# Revit family: 4068363 Lighting Fixture_Sylvania_Glace Square_Surface Mounted
name_source: partatom
category: Lighting Fixtures
revit_build: Autodesk Revit 2017 (Build: 20190507_1515(x64)
units: mm (PartAtom-declared; Revit-internal decimal feet)

## family parameters
Cut with Voids When Loaded = No
Host = Face
Light Source = Yes
OmniClass Number = 23.80.70.11.17
OmniClass Title = Specialized Lighting by Location or Use
Part Type = Normal
Room Calculation Point = No
Round Connector Dimension = Use Diameter
Shared = No

## types (1)
- Glace 3K HO Sq
    Accessory Material = Metal_Sylvania_Glace_Chrome
    Apparent Load = 16 VA
    Assembly Code = D5020200
    Body Marerial = Aluminum_Sylvania_Glace_Silver
    Catalog Number = 4068363 Glace 3K HO Sq
    Color Filter = 16777215
    Default Elevation = 0 mm  [stored 0 ft]
    Description = Super slim architectural design provides ultra modern minimalism with cutting-edge LED technology Utilises low power super efficient LED array providing perfect homogenous light distribution Superior fixture lumens when compared to existing 38W TC-DD Aesthetic round or square architectural form Wall and ceiling mounting Pendant option Microwave sensors with presence detection, lux and daylight management for optimum energy saving solutions 50,000 hrs life at 70% of the original output L70 Integral LED emergency options DALI dimming versions as standard Integral diffuser Ease of installation with Place and lock fixing mechanism The perfect solutions for corridors, modern circulation spaces and high end reception areas and foyers.
    Diameter = 240 mm  [stored 0.787402 ft]
    Diffuser Material = Acrylic_Sylvania_Glace_Opal
    Dimming Lamp Color Temperature Shift = <None>
    Drive Current = 700 mA
    Emit Shape Visible in Rendering = Yes
    Emit from Circle Diameter = 190 mm  [stored 0.62336 ft]
    Height = 54 mm  [stored 0.177165 ft]
    IK Rating = IK02
    IP Rating = IP20
    LOR = 100 %
    Lamp = Integrated LED
    Lamp Comments = 1 x 16W
    Length = 360 mm  [stored 1.1811 ft]
    Life = 50 000 h
    Manufacturer = Feilo Sylvania
    Model = Glace 3K HO Sq
    Photometric Web File = 4068363_Glace3KHOSq-162396.ies
    Product Family = GLACE - SQUARE
    Product Page URL = http://www.sylvania-lighting.com
    Tilt Angle = -90°
    URL = http://www.sylvania-lighting.com
    Voltage = 230 V
    Voltage Comments = UNV (Universal Voltage; 220-240 Volt)
    Weight = 2 kg
    Width = 360 mm  [stored 1.1811 ft]

note: [stored X ft] marks values corroborated as IEEE doubles in the binary element streams (Revit-internal decimal feet)

## geometry (parser evidence)
native form markers: Blend x6, Revolve x1, Sweep x1
no freeform markers — native parametric forms only
